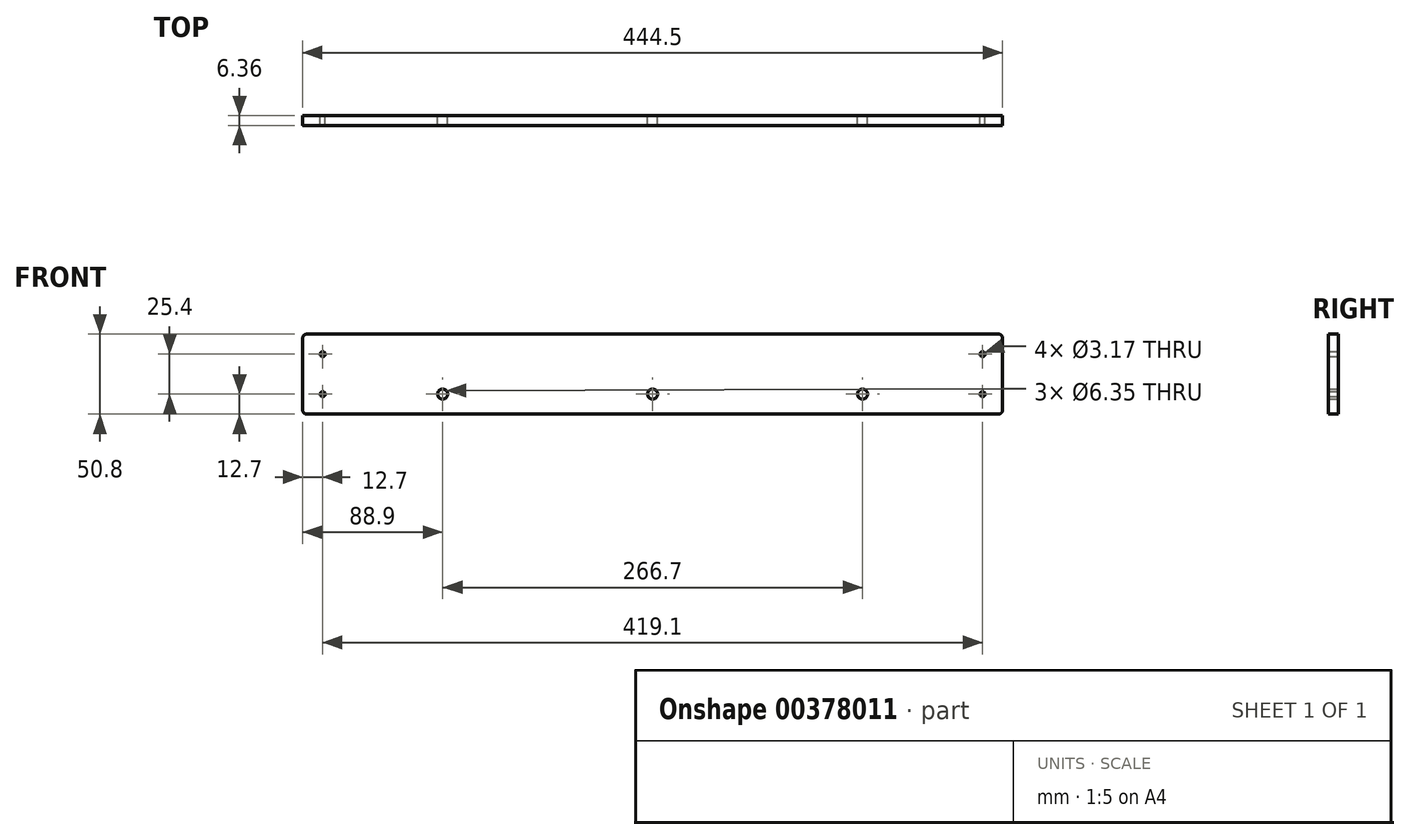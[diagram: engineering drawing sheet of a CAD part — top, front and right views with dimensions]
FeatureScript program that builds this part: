
annotation { "Feature Type Name" : "Feature", "Feature Type Description" : "" }
export const myFeature = defineFeature(function(context is Context, id is Id, definition is map)
    precondition{}
    {
        {
            var Q0;
            Q0=qCreatedBy(makeId("Front.planeOp"),FACE);
            var sketch = newSketch(context, id + "F0", { "sketchPlane" : qUnion([Q0])});
            skLineSegment(sketch, "E0.bottom", {"start": v(222.25, 25.4) * mm, "end": v(-222.25, 25.4) * mm});
            skLineSegment(sketch, "E0.top", {"start": v(222.25, -25.4) * mm, "end": v(-222.25, -25.4) * mm});
            skLineSegment(sketch, "E0.left", {"start": v(222.25, 25.4) * mm, "end": v(222.25, -25.4) * mm});
            skLineSegment(sketch, "E0.right", {"start": v(-222.25, 25.4) * mm, "end": v(-222.25, -25.4) * mm});
            skPoint(sketch, "E0.middle", {"position": v(0, 0) * mm});
            skLineSegment(sketch, "E1", {"start": v(196.85, 54.45) * mm, "end": v(196.85, -59.27) * mm, "construction": true});
            skLineSegment(sketch, "E2", {"start": v(261.02, -12.7) * mm, "end": v(-393.33, -12.7) * mm, "construction": true});
            skPoint(sketch, "E3", {"position": v(0, -12.7) * mm});
            skCircle(sketch, "E4", {"center": v(0, -12.7) * mm, "radius": 50.8 * mm, "construction": true});
            skCircle(sketch, "E5", {"center": v(133.35, -12.7) * mm, "radius": 50.8 * mm, "construction": true});
            skLineSegment(sketch, "E6", {"start": v(-196.85, 73.32) * mm, "end": v(-196.85, -60.42) * mm, "construction": true});
            skCircle(sketch, "E7", {"center": v(-133.35, -12.7) * mm, "radius": 50.8 * mm, "construction": true});
            skCircle(sketch, "E8", {"center": v(-133.35, -12.7) * mm, "radius": 3.18 * mm});
            skCircle(sketch, "E9", {"center": v(0, -12.7) * mm, "radius": 3.18 * mm});
            skCircle(sketch, "E10", {"center": v(133.35, -12.7) * mm, "radius": 3.18 * mm});
            skPoint(sketch, "E11", {"position": v(209.55, 12.7) * mm});
            skCircle(sketch, "E12", {"center": v(209.55, 12.7) * mm, "radius": 1.59 * mm});
            skPoint(sketch, "E13.MirrorP", {"position": v(209.55, -12.7) * mm});
            skCircle(sketch, "E14.MirrorC", {"center": v(209.55, -12.7) * mm, "radius": 1.59 * mm});
            skCircle(sketch, "E15.MirrorC", {"center": v(-209.55, -12.7) * mm, "radius": 1.59 * mm});
            skCircle(sketch, "E16.MirrorC", {"center": v(-209.55, 12.7) * mm, "radius": 1.59 * mm});
            skSolve(sketch);
        }
        {
            var Q0;
            Q0=makeQuery(id+"F0.imprint","IMPRINT",FACE,{"disambiguationData":[TD([[makeQuery(id+"F0.imprint","IMPRINT",EDGE,{"derivedFrom":sQuery(id+"F0.wireOp",EDGE,"E0.bottom")}),1.0]])]});
            extrude(context, id + "F1", {"entities" : qUnion([Q0]), "endBound" : BoundingType.SYMMETRIC, "depth" : 6.35 * mm});
        }
        {
            var Q0;
            Q0=makeQuery(id+"F1.opExtrude","SWEPT_EDGE",EDGE,{"disambiguationData":[OSD([sQuery(id+"F0.wireOp",EDGE,"E0.bottom"),sQuery(id+"F0.wireOp",EDGE,"E0.right")])]});
            var Q1;
            Q1=makeQuery(id+"F1.opExtrude","SWEPT_EDGE",EDGE,{"disambiguationData":[OSD([sQuery(id+"F0.wireOp",EDGE,"E0.top"),sQuery(id+"F0.wireOp",EDGE,"E0.right")])]});
            var Q2;
            Q2=makeQuery(id+"F1.opExtrude","SWEPT_EDGE",EDGE,{"disambiguationData":[OSD([sQuery(id+"F0.wireOp",EDGE,"E0.bottom"),sQuery(id+"F0.wireOp",EDGE,"E0.left")])]});
            var Q3;
            Q3=makeQuery(id+"F1.opExtrude","SWEPT_EDGE",EDGE,{"disambiguationData":[OSD([sQuery(id+"F0.wireOp",EDGE,"E0.top"),sQuery(id+"F0.wireOp",EDGE,"E0.left")])]});
            fillet(context, id + "F2", {"entities" : qUnion([Q0, Q1, Q2, Q3]), "radius" : 2.54 * mm, "tangentPropagation" : true, "allowEdgeOverflow" : false});
        }
    });
